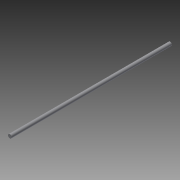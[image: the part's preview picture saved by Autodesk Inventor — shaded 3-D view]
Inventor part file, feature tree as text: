
AUTODESK INVENTOR PART (.ipt)
format: ipt  version: 2014 (Build 180170000, 170)  size: 64,512 bytes
history: native  units: mm
features: extrude x1, sketch x1
ambient origin geometry x8: Origin, YZ Plane, XZ Plane, XY Plane, X Axis, Y Axis, Z Axis, Center Point
bodies: Solid1 (feature_tree)
feature tree (2):
  extrude  "Extrusion1"  Depth=350.0mm TaperAngle=0.0deg
  sketch  "Sketch1"  dims[d0=8.0mm d1=350.0mm d2=0.0mm]
